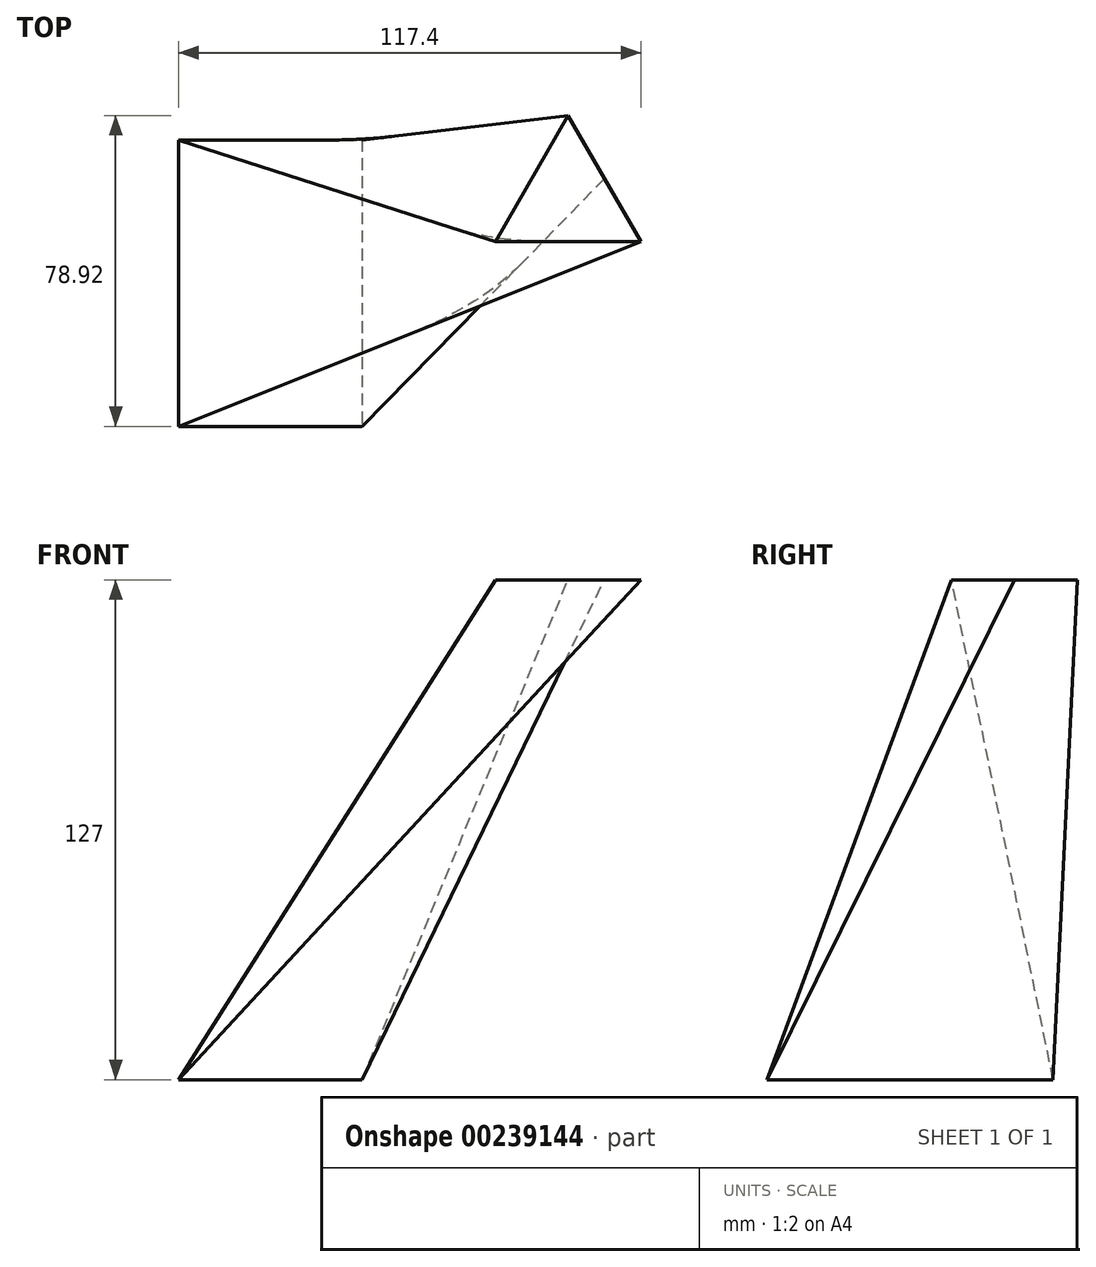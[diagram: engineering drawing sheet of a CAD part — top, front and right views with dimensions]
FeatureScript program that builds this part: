
annotation { "Feature Type Name" : "Feature", "Feature Type Description" : "" }
export const myFeature = defineFeature(function(context is Context, id is Id, definition is map)
    precondition{}
    {
        {
            var Q0;
            Q0=qCreatedBy(makeId("Top.planeOp"),FACE);
            cPlane(context, id + "F0", {"entities" : qUnion([Q0]), "cplaneType" : CPlaneType.OFFSET, "offset" : 127 * mm, "width" : 152.4 * mm, "height" : 152.4 * mm});
        }
        {
            var Q0;
            Q0=qCreatedBy(makeId("Top.planeOp"),FACE);
            var sketch = newSketch(context, id + "F1", { "sketchPlane" : qUnion([Q0])});
            skLineSegment(sketch, "E0.bottom", {"start": v(-58.87, 45.34) * mm, "end": v(-12.25, 45.34) * mm});
            skLineSegment(sketch, "E0.top", {"start": v(-58.87, -27.4) * mm, "end": v(-12.25, -27.4) * mm});
            skLineSegment(sketch, "E0.left", {"start": v(-58.87, 45.34) * mm, "end": v(-58.87, -27.4) * mm});
            skLineSegment(sketch, "E0.right", {"start": v(-12.25, 45.34) * mm, "end": v(-12.25, -27.4) * mm});
            skSolve(sketch);
        }
        {
            var Q0;
            Q0=qCreatedBy(id+"F0.planeOp",FACE);
            var sketch = newSketch(context, id + "F2", { "sketchPlane" : qUnion([Q0])});
            skLineSegment(sketch, "E1", {"start": v(40.04, 51.52) * mm, "end": v(21.56, 19.5) * mm});
            skLineSegment(sketch, "E2", {"start": v(21.56, 19.5) * mm, "end": v(58.53, 19.5) * mm});
            skLineSegment(sketch, "E3", {"start": v(58.53, 19.5) * mm, "end": v(40.04, 51.52) * mm});
            skSolve(sketch);
        }
        {
            var Q0;
            Q0 = qSketchRegion(id + "F1", true);
            var Q1;
            Q1 = qSketchRegion(id + "F2", true);
            loft(context, id + "F3", {"sheetProfilesArray" : [{ "sheetProfileEntities" : qUnion([Q0]) }, { "sheetProfileEntities" : qUnion([Q1]) }]});
        }
    });
